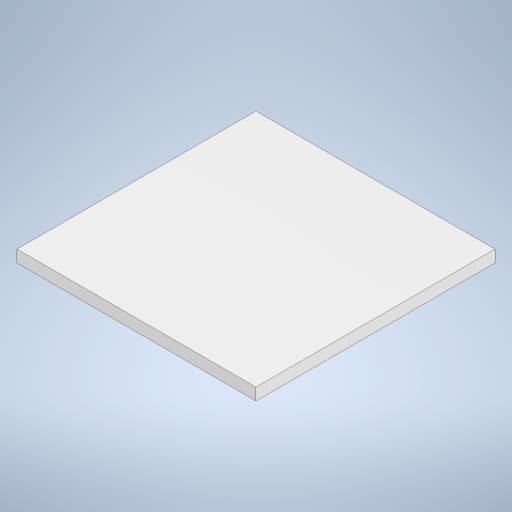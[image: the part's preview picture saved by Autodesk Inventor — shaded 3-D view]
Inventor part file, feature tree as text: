
AUTODESK INVENTOR PART (.ipt)
format: ipt  version: 2024.2 (Build 282272000, 272)  size: 202,240 bytes
history: native  units: in
note: dims shown in document units (in); Inventor stores cm internally (conversion verified against a paired STEP export)
features: extrude x1, sketch x1
ambient origin geometry x8: Origin, YZ Plane, XZ Plane, XY Plane, X Axis, Y Axis, Z Axis, Center Point
bodies: Solid1 (feature_tree)
feature tree (2):
  extrude  "Extrusion1"  Depth=5.0in
  sketch  "Sketch1"  dims[d0=5.0in d1=5.0in d2=0.25in d3=0.0in]
